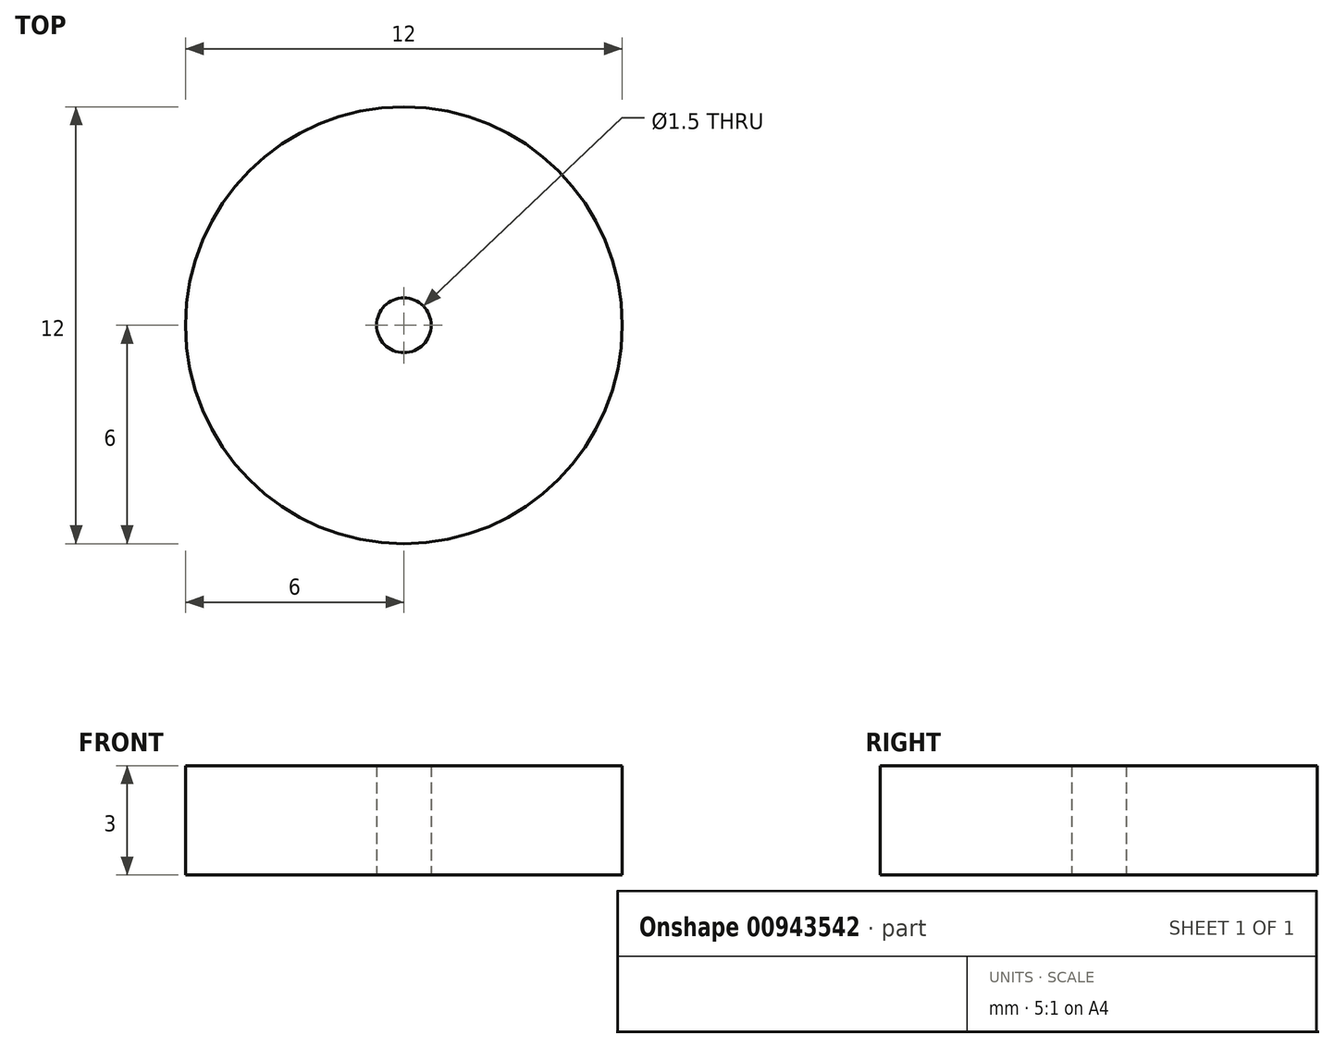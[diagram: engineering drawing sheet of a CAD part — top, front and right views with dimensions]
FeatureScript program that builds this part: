
annotation { "Feature Type Name" : "Feature", "Feature Type Description" : "" }
export const myFeature = defineFeature(function(context is Context, id is Id, definition is map)
    precondition{}
    {
        {
            var Q0;
            Q0=qCreatedBy(makeId("Top.planeOp"),FACE);
            var sketch = newSketch(context, id + "F0", { "sketchPlane" : qUnion([Q0])});
            skCircle(sketch, "E0", {"center": v(0, 0) * mm, "radius": 6 * mm});
            skCircle(sketch, "E1", {"center": v(0, 0) * mm, "radius": 0.75 * mm});
            skSolve(sketch);
        }
        {
            var Q0;
            Q0=makeQuery(id+"F0.imprint","IMPRINT",FACE,{"disambiguationData":[TD([[makeQuery(id+"F0.imprint","IMPRINT",EDGE,{"derivedFrom":sQuery(id+"F0.wireOp",EDGE,"E0")}),1.0]])]});
            extrude(context, id + "F1", {"entities" : qUnion([Q0]), "depth" : 3 * mm, "offsetDistance" : 25 * mm});
        }
    });
